# Revit family: Thorn ALTIS GEN5 Gearbox-Premium-class C5 with NTC
name_source: partatom
category: Electrical Fixtures
units: mm (PartAtom-declared; Revit-internal decimal feet)

## family parameters
Cut with Voids When Loaded = Yes
Host = Face
Maintain Annotation Orientation = No
Part Type = Normal
Room Calculation Point = Yes
Round Connector Dimension = Use Diameter
Shared = Yes

## types (20) — shared parameters
Assembly Code = Pr_60_70_48_54
Description = LED control gear
Export Type to IFC As = IfcLightFixtureType
Lamp = LED
Luminaire Height = 120 mm  [stored 0.393701 ft]
Luminaire Length = 500 mm  [stored 1.64042 ft]
Luminaire Width = 150 mm
Manufacturer = Thorn Lighting
Material Housing = Thorn-Aluminium-RAL 7043-Traffic Grey B
Power Factor = 1
Type IFC Predefined Type = DIRECTIONSOURCE
Type Image = TLG_ALT5_F_GB.jpg
URL = https://www.thornlighting.com
zero-valued in all types: Default Elevation

## per-type parameters (varying)
| type | Apparent Load | Model | Wattage |
| ALG5 GB 1368W 0.70A 565V 2CH DA | 1368 VA | 96671933 | 1368 W |
| ALG5 GB 1368W 0.70A 565V 2CH RDMX | 1368 VA | 96671943 | 1368 W |
| ALG5 GB 1368W 0.85A 565V 2CH DA | 1368 VA | 96671932 | 1368 W |
| ALG5 GB 1368W 0.85A 565V 2CH RDMX | 1368 VA | 96671942 | 1368 W |
| ALG5 GB 1368W 1.05A 565V 2CH DA | 1368 VA | 96671931 | 1368 W |
| ALG5 GB 1368W 1.05A 565V 2CH RDMX | 1368 VA | 96671941 | 1368 W |
| ALG5 GB 1368W 1.25A 565V 2CH DA | 1368 VA | 96671930 | 1368 W |
| ALG5 GB 1368W 1.25A 565V 2CH RDMX | 1368 VA | 96671940 | 1368 W |
| ALG5 GB 1368W 1.40A 565V 2CH DA | 1368 VA | 96671929 | 1368 W |
| ALG5 GB 1368W 1.40A 565V 2CH RDMX | 1368 VA | 96671939 | 1368 W |
| ALG5 GB 2052W 0.70A 565V 3CH DA | 2052 VA | 96671928 | 2052 W |
| ALG5 GB 2052W 0.70A 565V 3CH RDMX | 2052 VA | 96671938 | 2052 W |
| ALG5 GB 2052W 0.85A 565V 3CH DA | 2052 VA | 96671927 | 2052 W |
| ALG5 GB 2052W 0.85A 565V 3CH RDMX | 2052 VA | 96671937 | 2052 W |
| ALG5 GB 2052W 1.05A 565V 3CH DA | 2052 VA | 96671926 | 2052 W |
| ALG5 GB 2052W 1.05A 565V 3CH RDMX | 2052 VA | 96671936 | 2052 W |
| ALG5 GB 2052W 1.25A 565V 3CH DA | 2052 VA | 96671925 | 2052 W |
| ALG5 GB 2052W 1.25A 565V 3CH RDMX | 2052 VA | 96671935 | 2052 W |
| ALG5 GB 2052W 1.40A 565V 3CH DA | 2052 VA | 96671924 | 2052 W |
| ALG5 GB 2052W 1.40A 565V 3CH RDMX | 2052 VA | 96671934 | 2052 W |

note: [stored X ft] marks values corroborated as IEEE doubles in the binary element streams (Revit-internal decimal feet)

## geometry (parser evidence)
native form markers: Sweep x2
no freeform markers — native parametric forms only
